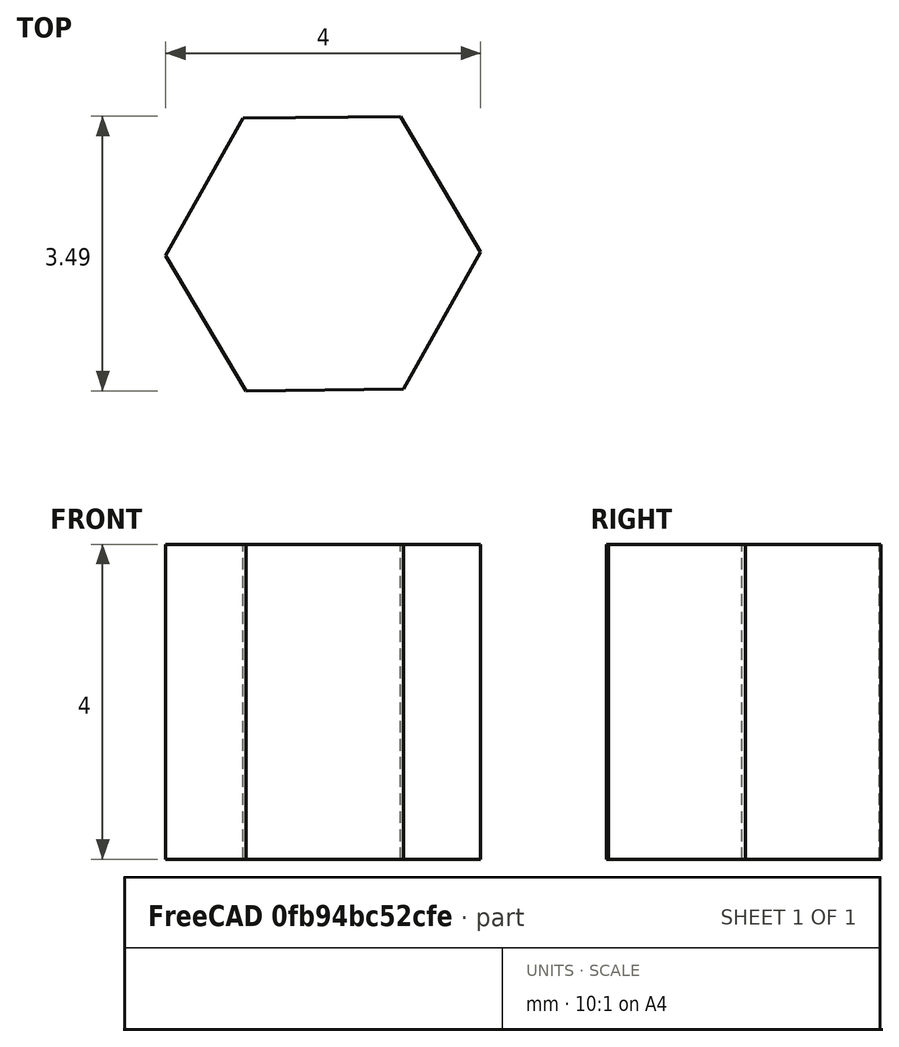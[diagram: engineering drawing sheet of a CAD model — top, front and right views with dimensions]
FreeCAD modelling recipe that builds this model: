
FCSTD DOCUMENT  (FreeCAD 0.18.4R)
Label: Magnet_2mm_4mm
License: All rights reserved
LicenseURL: http://en.wikipedia.org/wiki/All_rights_reserved
objects: TechDraw::DrawViewPart×5, TechDraw::DrawViewDimension×4, Sketcher::SketchObject×2, TechDraw::DrawSVGTemplate×2, TechDraw::DrawPage×2, PartDesign::Pad×1, PartDesign::Body×1
note: 5 computed .brp shape members not serialized (recipe doc carries the construction recipe); baked Part::Feature solids carry a one-line shape summary decoded from their .brp

FEATURE [Sketcher::SketchObject] Sketch
FEATURE [Sketcher::SketchObject] Sketch001
  MapMode = 5
  Support = -> [XY_Plane]
  sketch-geometry (7):
    g0: LineSegment StartX=-6.01106 StartY=3.14248 StartZ=0 EndX=-5.02939 EndY=4.88498 EndZ=0
    g1: LineSegment StartX=-5.02939 StartY=4.88498 StartZ=0 EndX=-6.04761 EndY=6.60638 EndZ=0
    g2: LineSegment StartX=-6.04761 StartY=6.60638 StartZ=0 EndX=-8.0475 EndY=6.58528 EndZ=0
    g3: LineSegment StartX=-8.0475 StartY=6.58528 StartZ=0 EndX=-9.02917 EndY=4.84277 EndZ=0
    g4: LineSegment StartX=-9.02917 StartY=4.84277 StartZ=0 EndX=-8.01094 EndY=3.12137 EndZ=0
    g5: LineSegment StartX=-8.01094 StartY=3.12137 StartZ=0 EndX=-6.01106 EndY=3.14248 EndZ=0
    g6: Circle [constr] CenterX=-7.02928 CenterY=4.86388 CenterZ=0 NormalX=0 NormalY=0 NormalZ=1 AngleXU=0 Radius=2
  constraints (14):
    c: Coincident(g0,g1)
    c: Coincident(g1,g2)
    c: Coincident(g2,g3)
    c: Coincident(g3,g4)
    c: Coincident(g4,g5)
    c: Coincident(g5,g0)
    c: Equal(g0, g1-g5) x5
    c: PointOnObject(g0,g6)
    c: PointOnObject(g1,g6)
    c: PointOnObject(g2,g6)
    c: PointOnObject(g3,g6)
    c: PointOnObject(g4,g6)
    c: PointOnObject(g5,g6)
    c: Distance(g1) = 2
FEATURE [PartDesign::Pad] Pad
  Length = 4
  Length2 = 100
  Profile = -> Sketch001
  Type = 0
FEATURE [PartDesign::Body] Body
  Group = -> [Sketch001,Pad]
  Origin = -> Origin
  Tip = -> Pad
FEATURE [TechDraw::DrawSVGTemplate] Template
  EditableTexts = Designed_by_Name=Designed by Melanie; Drawing_number=001; FC-Date=09/30/20; FC-Title=Magnet 2mm by 4mm
  Height = 210
  Orientation = 1
  Width = 297
FEATURE [TechDraw::DrawViewPart] View
  CoarseView = false
  Direction = (0.577,-0.577,0.577)
  Focus = 100
  HardHidden = false
  IsoCount = 0
  IsoHidden = false
  IsoVisible = false
  LockPosition = false
  Perspective = false
  Rotation = 0
  ScaleType = 0
  SeamHidden = false
  SeamVisible = false
  SmoothHidden = false
  SmoothVisible = false
  Source = -> [Body]
  X = 148.5
  Y = 105
FEATURE [TechDraw::DrawPage] Page
  KeepUpdated = true
  ProjectionType = 0
  Template = -> Template
  Views = -> [View]
FEATURE [TechDraw::DrawSVGTemplate] Template001
  EditableTexts = AUTHOR_NAME=Melanie Allen; DN=001; DRAWING_TITLE=Magnet 2mm by 4mm; FC-DATE=10/05/2020; FC-REV=REV B; FC-SC=10; FC-SH=X / Y; FC-SI=A4
  Height = 297
  Orientation = 0
  Width = 210
FEATURE [TechDraw::DrawViewPart] View001  label="View002"
  CoarseView = false
  Direction = (0,-1,0)
  Focus = 100
  HardHidden = false
  IsoCount = 0
  IsoHidden = false
  IsoVisible = false
  LockPosition = false
  Perspective = false
  Rotation = 0
  Scale = 10
  ScaleType = 0
  SeamHidden = false
  SeamVisible = false
  SmoothHidden = false
  SmoothVisible = false
  Source = -> [Body]
  X = 150
  Y = 220
FEATURE [TechDraw::DrawViewPart] View002  label="View003"
  CoarseView = false
  Direction = (0,0,1)
  Focus = 100
  HardHidden = false
  IsoCount = 0
  IsoHidden = false
  IsoVisible = false
  LockPosition = false
  Perspective = false
  Rotation = 0
  Scale = 10
  ScaleType = 0
  SeamHidden = false
  SeamVisible = false
  SmoothHidden = false
  SmoothVisible = false
  Source = -> [Body]
  X = 70
  Y = 120
FEATURE [TechDraw::DrawViewPart] View003  label="View001"
  CoarseView = false
  Direction = (-1,0,0)
  Focus = 100
  HardHidden = false
  IsoCount = 0
  IsoHidden = false
  IsoVisible = false
  LockPosition = false
  Perspective = false
  Rotation = 0
  Scale = 10
  ScaleType = 0
  SeamHidden = false
  SeamVisible = false
  SmoothHidden = false
  SmoothVisible = false
  Source = -> [Body]
  X = 70
  Y = 220
FEATURE [TechDraw::DrawViewPart] View004
  CoarseView = false
  Direction = (0.577,-0.577,0.577)
  Focus = 100
  HardHidden = false
  IsoCount = 0
  IsoHidden = false
  IsoVisible = false
  LockPosition = false
  Perspective = false
  Rotation = 0
  Scale = 10
  ScaleType = 0
  SeamHidden = false
  SeamVisible = false
  SmoothHidden = false
  SmoothVisible = false
  Source = -> [Body]
  X = 150
  Y = 120
FEATURE [TechDraw::DrawViewDimension] Dimension
  Arbitrary = false
  FormatSpec = %.2f
  LockPosition = false
  MeasureType = 1
  OverTolerance = 0
  References2D = -> [View002]
  Rotation = 0
  ScaleType = 0
  Type = 0
  UnderTolerance = 0
  X = 0.812405
  Y = 28.78
FEATURE [TechDraw::DrawViewDimension] Dimension001
  Arbitrary = false
  FormatSpec = %.2f
  LockPosition = false
  MeasureType = 1
  OverTolerance = 0
  References2D = -> [View004]
  Rotation = 0
  ScaleType = 0
  Type = 0
  UnderTolerance = 0
  X = -34.043
  Y = -2.24209
FEATURE [TechDraw::DrawViewDimension] Dimension002
  Arbitrary = false
  FormatSpec = %.2f
  LockPosition = false
  MeasureType = 1
  OverTolerance = 0
  References2D = -> [View002]
  Rotation = 0
  ScaleType = 0
  Type = 2
  UnderTolerance = 0
  X = -39.8307
  Y = -4.54856
FEATURE [TechDraw::DrawViewDimension] Dimension003
  Arbitrary = false
  FormatSpec = %.2f
  LockPosition = false
  MeasureType = 1
  OverTolerance = 0
  References2D = -> [View002]
  Rotation = 0
  ScaleType = 0
  Type = 1
  UnderTolerance = 0
  X = -2.39241
  Y = 42.038
FEATURE [TechDraw::DrawPage] Page001
  KeepUpdated = true
  ProjectionType = 0
  Template = -> Template001
  Views = -> [View001,View002,View003,View004,Dimension,Dimension001,Dimension002,Dimension003]
